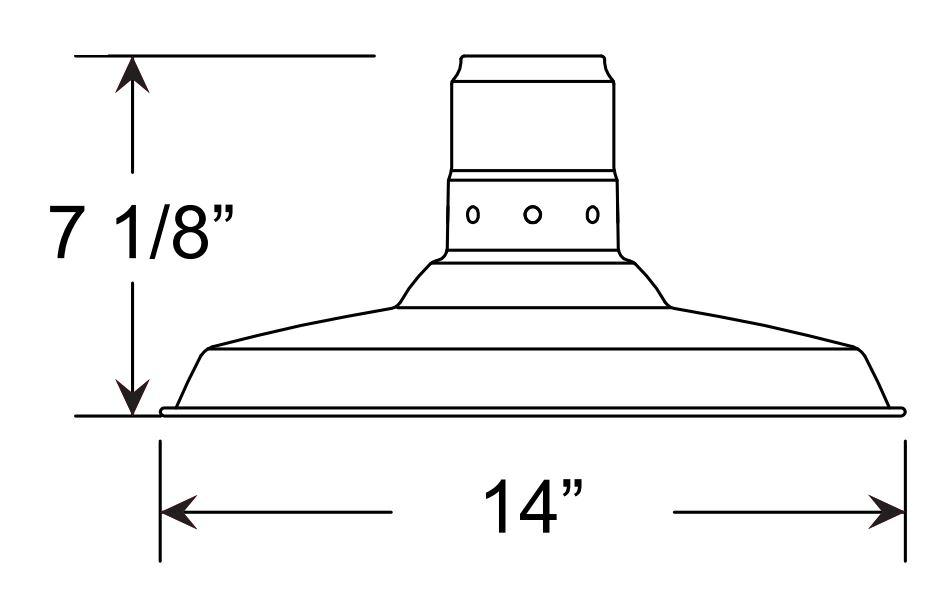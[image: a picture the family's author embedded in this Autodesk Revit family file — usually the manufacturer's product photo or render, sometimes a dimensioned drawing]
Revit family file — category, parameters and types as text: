
# Revit family: Warehouse MB 8,10,12,14,16,18,20,24,27
name_source: partatom
category: Lighting Fixtures
units: mm (PartAtom-declared; Revit-internal decimal feet)

## family parameters
Always vertical = Yes
Cut with Voids When Loaded = No
Light Source = Yes
OmniClass Number = 23.80.70.00
OmniClass Title = Lighting
Part Type = Normal
Room Calculation Point = No
Round Connector Dimension = Use Diameter
Shared = No
Work Plane-Based = No

## types (9) — shared parameters
BULB = Yes
Body Colour = Spun aluminium
Body Material = body
Bulb = Bulb
CRI = >90
Canopy Body = Texture Black
Color Filter = 16777215
Construction Material = Heavy Duty spun aluminum.
Default Elevation = 0' - 0"
Description = 120-277 Voltage
Dimming = 1%
Dimming Lamp Color Temperature Shift = <None>
Efficiency = 65-125 lumens per watt
Lamp = MB
Life = L70 50,000 hours
Load Classification = Lighting
Manufacturer = ANP Lighting
Power Factor = 1
Tilt Angle = 90.00°
URL = https://www.anplighting.com
Voltage = 277 V
Warranty = 5 year limited warranty

## per-type parameters (varying)
| type | Apparent Load | Fixture Diameter | Fixture Height | Photometric Web File | W508 | W510 | W512 | W514 | W516 | W518 | W520 | W524 | W527 | Wattage Comments | Weight | a | b |
| W508 | 100 VA | 0' - 8" | 0' - 7" | W508M009LDNW40K.IES | Yes | No | No | No | No | No | No | No | No | 100 W Max | 1.0 lb | 0' - 7" | 0' - 2" |
| W510 | 100 VA | 0' - 10" | 0' - 6 1/2" | W510M010LDDW40K.IES | No | Yes | No | No | No | No | No | No | No | 100 W Max | 1.0 lb | 0' - 6 1/2" | 0' - 2" |
| W512 | 150 VA | 1' - 0 1/4" | 0' - 7 1/4" | W510M010LDDW40K.IES | No | No | Yes | No | No | No | No | No | No | 150 W Max | 1.0 lb | 0' - 7 1/4" | 0' - 2" |
| W514 | 150 VA | 1' - 2 3/4" | 0' - 7 1/4" | W514-100GLCL-32WPL-T15295-.ies | No | No | No | Yes | No | No | No | No | No | 150 W Max | 1.5 lbs | 0' - 7 1/4" | 0' - 2" |
| W516 | 200 VA | 1' - 4" | 0' - 8 3/4" | W516M016LDNW40K.IES | No | No | No | No | Yes | No | No | No | No | 200 W Max | 1.5 lbs | 0' - 8 3/4" | 0' - 2" |
| W518 | 200 VA | 1' - 6" | 0' - 9" | W518-100INC-T15300.IES | No | No | No | No | No | Yes | No | No | No | 200 W Max | 2.0 lbs | 0' - 9" | 0' - 2" |
| W520 | 200 VA | 1' - 8" | 0' - 10" | W520M024LDDW40K.IES | No | No | No | No | No | No | Yes | No | No | 200 W Max | 2.5 lbs | 0' - 10" | 0' - 2" |
| W524 | 200 VA | 2' - 0 1/4" | 1' - 3 1/2" | W520M024LDDW40K.IES | No | No | No | No | No | No | No | Yes | No | 200 W Max | 5.5 lbs | 1' - 3 1/2" | 0' - 3" |
| W527 | 200 VA | 2' - 3" | 1' - 4" | W527M037LDDW40K.IES | No | No | No | No | No | No | No | No | Yes | 200 W Max | 6.0 lbs | 1' - 4" | 0' - 3" |

note: column(s) folded — value = type name in every type: Model

## geometry (parser evidence)
native form markers: Sweep x51
no freeform markers — native parametric forms only
